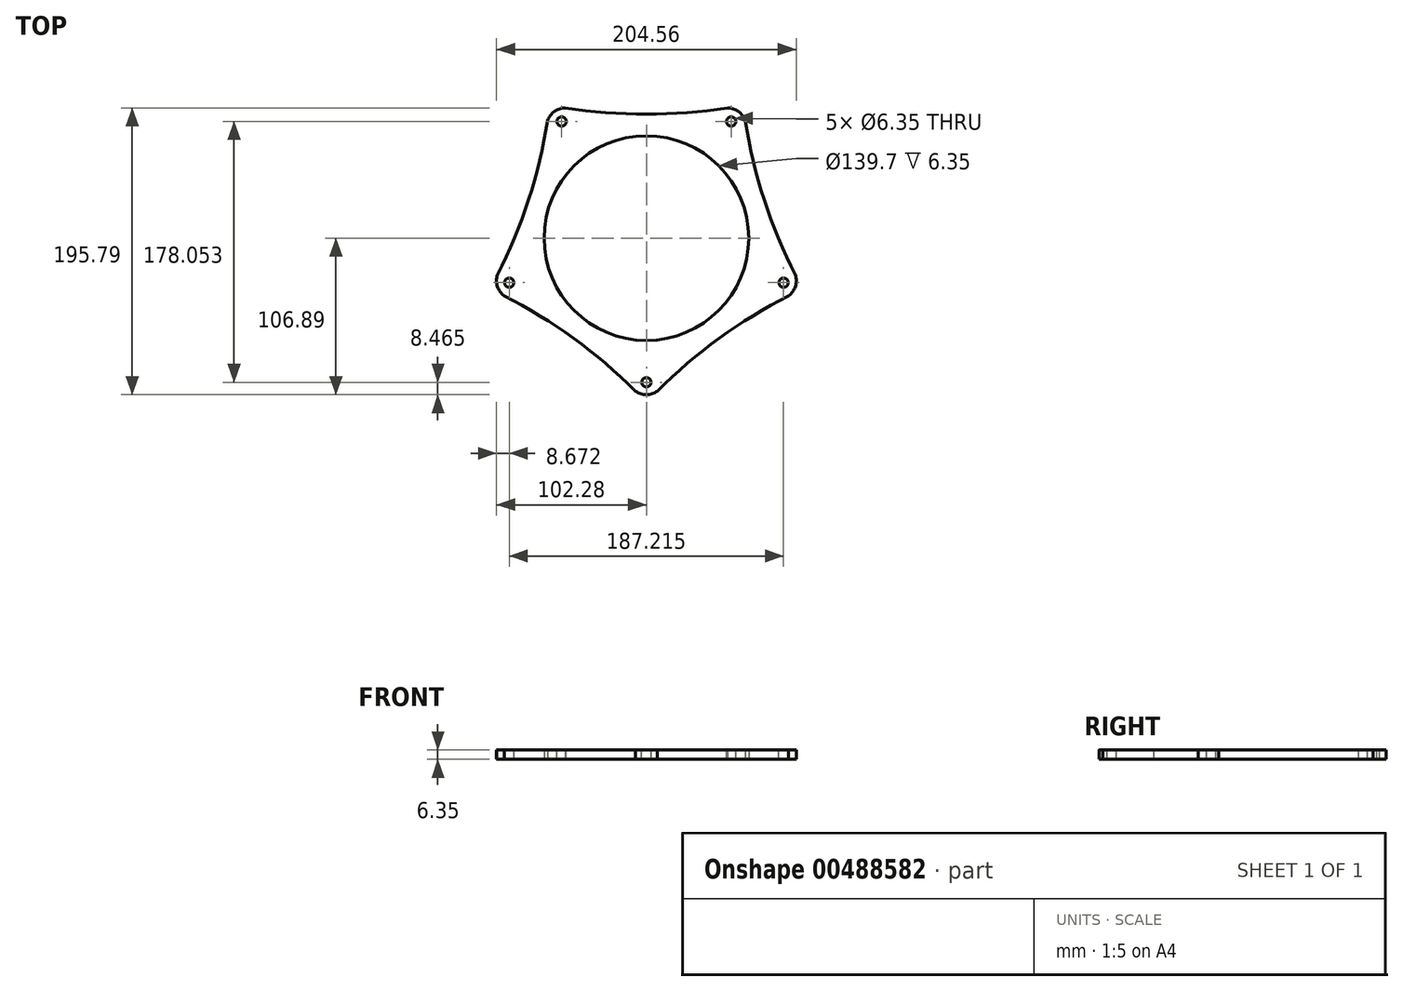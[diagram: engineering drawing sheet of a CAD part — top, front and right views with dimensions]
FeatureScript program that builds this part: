
annotation { "Feature Type Name" : "Feature", "Feature Type Description" : "" }
export const myFeature = defineFeature(function(context is Context, id is Id, definition is map)
    precondition{}
    {
        {
            var Q0;
            Q0=qCreatedBy(makeId("Top.planeOp"),FACE);
            var sketch = newSketch(context, id + "F0", { "sketchPlane" : qUnion([Q0])});
            skCircle(sketch, "E0.cCircle", {"center": v(0, 0) * mm, "radius": 88.9 * mm, "construction": true});
            skLineSegment(sketch, "E0.0", {"start": v(-64.59, 88.9) * mm, "end": v(64.59, 88.9) * mm});
            skLineSegment(sketch, "E0.1", {"start": v(64.59, 88.9) * mm, "end": v(104.5, -33.96) * mm});
            skLineSegment(sketch, "E0.2", {"start": v(104.5, -33.96) * mm, "end": v(0, -109.89) * mm});
            skLineSegment(sketch, "E0.3", {"start": v(0, -109.89) * mm, "end": v(-104.5, -33.96) * mm});
            skLineSegment(sketch, "E0.4", {"start": v(-104.5, -33.96) * mm, "end": v(-64.59, 88.9) * mm});
            skPoint(sketch, "E0.0.midPoint", {"position": v(0, 88.9) * mm});
            skCircle(sketch, "E1", {"center": v(0, 0) * mm, "radius": 69.85 * mm});
            skSolve(sketch);
        }
        {
            var Q0;
            Q0 = qSketchRegion(id + "F0", true);
            extrude(context, id + "F1", {"entities" : qUnion([Q0]), "depth" : 6.35 * mm});
        }
        {
            var Q0;
            Q0=makeQuery(id+"F1.opExtrude","SWEPT_EDGE",EDGE,{"disambiguationData":[OSD([sQuery(id+"F0.wireOp",EDGE,"E0.0"),sQuery(id+"F0.wireOp",EDGE,"E0.4")])]});
            var Q1;
            Q1=makeQuery(id+"F1.opExtrude","SWEPT_EDGE",EDGE,{"disambiguationData":[OSD([sQuery(id+"F0.wireOp",EDGE,"E0.3"),sQuery(id+"F0.wireOp",EDGE,"E0.4")])]});
            var Q2;
            Q2=makeQuery(id+"F1.opExtrude","SWEPT_EDGE",EDGE,{"disambiguationData":[OSD([sQuery(id+"F0.wireOp",EDGE,"E0.2"),sQuery(id+"F0.wireOp",EDGE,"E0.3")])]});
            var Q3;
            Q3=makeQuery(id+"F1.opExtrude","SWEPT_EDGE",EDGE,{"disambiguationData":[OSD([sQuery(id+"F0.wireOp",EDGE,"E0.1"),sQuery(id+"F0.wireOp",EDGE,"E0.2")])]});
            var Q4;
            Q4=makeQuery(id+"F1.opExtrude","SWEPT_EDGE",EDGE,{"disambiguationData":[OSD([sQuery(id+"F0.wireOp",EDGE,"E0.0"),sQuery(id+"F0.wireOp",EDGE,"E0.1")])]});
            fillet(context, id + "F2", {"entities" : qUnion([Q0, Q1, Q2, Q3, Q4]), "radius" : 12.7 * mm, "tangentPropagation" : true, "allowEdgeOverflow" : false});
        }
        {
            var Q0;
            Q0=makeQuery(id+"F1.opExtrude","CAP_FACE",FACE,{"disambiguationData":[OSD([sQuery(id+"F0.wireOp",EDGE,"E0.0"),sQuery(id+"F0.wireOp",EDGE,"E0.1"),sQuery(id+"F0.wireOp",EDGE,"E0.2"),sQuery(id+"F0.wireOp",EDGE,"E0.3"),sQuery(id+"F0.wireOp",EDGE,"E0.4"),sQuery(id+"F0.wireOp",EDGE,"E1")])],"isStart":false});
            var sketch = newSketch(context, id + "F3", { "sketchPlane" : qUnion([Q0])});
            skCircle(sketch, "E2", {"center": v(0, 0) * mm, "radius": 98.43 * mm, "construction": true});
            skLineSegment(sketch, "E3", {"start": v(0, -106.89) * mm, "end": v(0, 0) * mm, "construction": true});
            skCircle(sketch, "E4", {"center": v(0, -98.43) * mm, "radius": 3.18 * mm});
            skCircle(sketch, "E5.1.0", {"center": v(93.6, -30.41) * mm, "radius": 3.18 * mm});
            skCircle(sketch, "E5.2.0", {"center": v(57.85, 79.63) * mm, "radius": 3.18 * mm});
            skCircle(sketch, "E5.3.0", {"center": v(-57.85, 79.63) * mm, "radius": 3.18 * mm});
            skCircle(sketch, "E5.4.0", {"center": v(-93.6, -30.41) * mm, "radius": 3.18 * mm});
            skSolve(sketch);
        }
        {
            var Q0;
            Q0 = qSketchRegion(id + "F3", true);
            extrude(context, id + "F4", {"entities" : qUnion([Q0]), "operationType" : NewBodyOperationType.REMOVE, "endBound" : BoundingType.UP_TO_NEXT, "oppositeDirection" : true, "depth" : 25.4 * mm});
        }
        {
            var Q0;
            Q0=makeQuery(id+"F1.opExtrude","CAP_FACE",FACE,{"disambiguationData":[OSD([sQuery(id+"F0.wireOp",EDGE,"E0.0"),sQuery(id+"F0.wireOp",EDGE,"E0.1"),sQuery(id+"F0.wireOp",EDGE,"E0.2"),sQuery(id+"F0.wireOp",EDGE,"E0.3"),sQuery(id+"F0.wireOp",EDGE,"E0.4"),sQuery(id+"F0.wireOp",EDGE,"E1")])],"isStart":false});
            var sketch = newSketch(context, id + "F5", { "sketchPlane" : qUnion([Q0])});
            skArc(sketch, "E6", {"start": v(-55.36, 88.9) * mm, "mid": v(0, 84.56) * mm, "end": v(55.36, 88.9) * mm});
            skLineSegment(sketch, "E7", {"start": v(-55.36, 88.9) * mm, "end": v(55.36, 88.9) * mm});
            skPoint(sketch, "E8.center", {"position": v(-0.22, -0.69) * mm});
            skLineSegment(sketch, "E9", {"start": v(-67.44, 80.12) * mm, "end": v(-101.66, -25.18) * mm});
            skLineSegment(sketch, "E10", {"start": v(-97.04, -39.38) * mm, "end": v(-7.46, -104.46) * mm});
            skLineSegment(sketch, "E11", {"start": v(7.46, -104.46) * mm, "end": v(97.04, -39.38) * mm});
            skLineSegment(sketch, "E12", {"start": v(101.66, -25.18) * mm, "end": v(67.44, 80.12) * mm});
            skArc(sketch, "E13", {"start": v(67.44, 80.12) * mm, "mid": v(80.43, 26.13) * mm, "end": v(101.66, -25.18) * mm});
            skArc(sketch, "E14", {"start": v(97.04, -39.38) * mm, "mid": v(49.7, -68.41) * mm, "end": v(7.46, -104.46) * mm});
            skArc(sketch, "E15", {"start": v(-7.46, -104.46) * mm, "mid": v(-49.7, -68.41) * mm, "end": v(-97.04, -39.38) * mm});
            skArc(sketch, "E16", {"start": v(-101.66, -25.18) * mm, "mid": v(-80.43, 26.13) * mm, "end": v(-67.44, 80.12) * mm});
            skSolve(sketch);
        }
        {
            var Q0;
            Q0 = qSketchRegion(id + "F5", true);
            extrude(context, id + "F6", {"entities" : qUnion([Q0]), "operationType" : NewBodyOperationType.REMOVE, "endBound" : BoundingType.UP_TO_NEXT, "oppositeDirection" : true, "depth" : 25.4 * mm});
        }
    });
